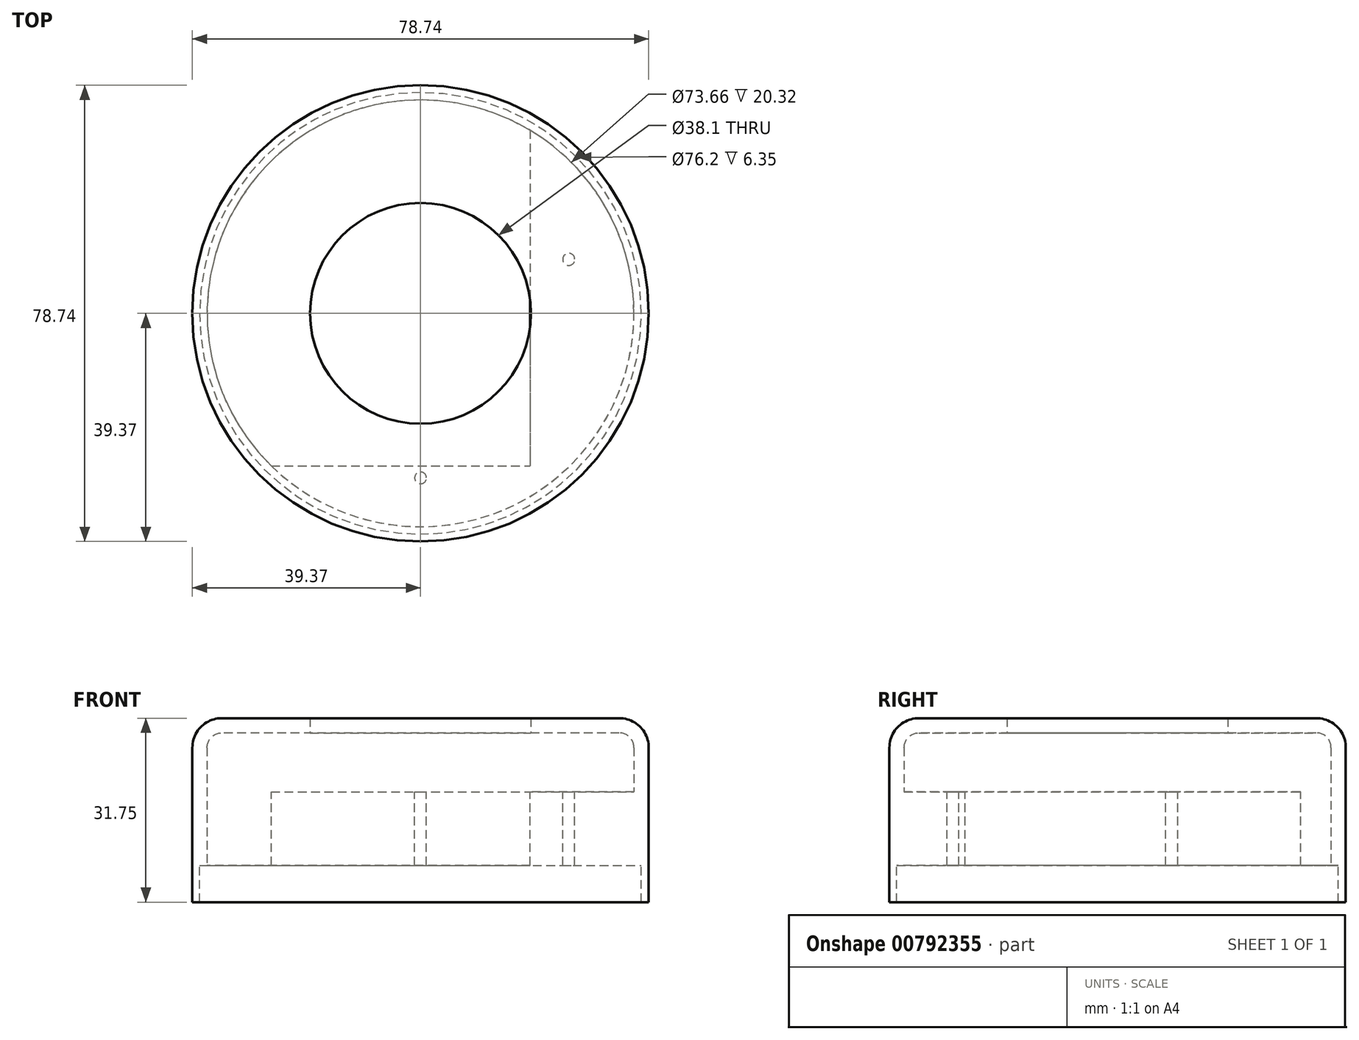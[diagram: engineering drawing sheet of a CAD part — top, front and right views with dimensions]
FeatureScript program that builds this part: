
annotation { "Feature Type Name" : "Feature", "Feature Type Description" : "" }
export const myFeature = defineFeature(function(context is Context, id is Id, definition is map)
    precondition{}
    {
        {
            var Q0;
            Q0=qCreatedBy(makeId("Top.planeOp"),FACE);
            var sketch = newSketch(context, id + "F0", { "sketchPlane" : qUnion([Q0])});
            skCircle(sketch, "E0", {"center": v(0, 0) * mm, "radius": 39.37 * mm});
            skSolve(sketch);
        }
        {
            var Q0;
            Q0 = qSketchRegion(id + "F0", true);
            extrude(context, id + "F1", {"entities" : qUnion([Q0]), "depth" : 12.7 * mm, "offsetDistance" : 25.4 * mm});
        }
        {
            var Q0;
            Q0=makeQuery(id+"F1.opExtrude","CAP_FACE",FACE,{"disambiguationData":[OSD([sQuery(id+"F0.wireOp",EDGE,"E0")])],"isStart":true});
            shell(context, id + "F2", {"entities" : qUnion([Q0]), "thickness" : 2.54 * mm});
        }
        {
            var Q0;
            Q0=makeQuery(id+"F1.opExtrude","CAP_EDGE",EDGE,{"disambiguationData":[OSD([sQuery(id+"F0.wireOp",EDGE,"E0")])],"isStart":false});
            fillet(context, id + "F3", {"entities" : qUnion([Q0]), "radius" : 5.08 * mm, "tangentPropagation" : true, "allowEdgeOverflow" : false});
        }
        {
            var Q0;
            Q0=makeQuery(id+"F0arPh6gx08AXpp_1.opExtrude","CAP_EDGE",EDGE,{"disambiguationData":[OSD([sQuery(id+"FFaWsDePzQ0D9wn_1.wireOp",EDGE,"ae57389e-1940-4f7f-8b4d-1324cf397c20.2.0")])],"isStart":true});
            var Q1;
            Q1=makeQuery(id+"F0arPh6gx08AXpp_1.opExtrude","CAP_EDGE",EDGE,{"disambiguationData":[OSD([sQuery(id+"FFaWsDePzQ0D9wn_1.wireOp",EDGE,"ae57389e-1940-4f7f-8b4d-1324cf397c20.1.0")])],"isStart":true});
            var Q2;
            Q2=makeQuery(id+"F0arPh6gx08AXpp_1.opExtrude","CAP_EDGE",EDGE,{"disambiguationData":[OSD([sQuery(id+"FFaWsDePzQ0D9wn_1.wireOp",EDGE,"ae57389e-1940-4f7f-8b4d-1324cf397c20.3.0")])],"isStart":true});
            var Q3;
            Q3=makeQuery(id+"F0arPh6gx08AXpp_1.opExtrude","CAP_EDGE",EDGE,{"disambiguationData":[OSD([sQuery(id+"FFaWsDePzQ0D9wn_1.wireOp",EDGE,"xz74w6c5-Paq0-shCl-McQr-9mFM74ZJmCNI")])],"isStart":true});
            var Q4;
            {var subQ0=sQuery(id+"F0.wireOp",EDGE,"E0");Q4=makeQuery(id+"F2.opShell","OFFSET_EDGE",EDGE,{"disambiguationData":[OSD([subQ0]),TDD([makeQuery(id+"F1.opExtrude","CAP_EDGE",EDGE,{"disambiguationData":[OSD([subQ0])],"isStart":false})])]});}
            fillet(context, id + "F4", {"entities" : qUnion([Q0, Q1, Q2, Q3, Q4]), "radius" : 2.54 * mm, "tangentPropagation" : true, "allowEdgeOverflow" : false});
        }
        {
            var Q0;
            {var subQ0=sQuery(id+"F0.wireOp",EDGE,"E0");Q0=makeQuery(id+"F0arPh6gx08AXpp_1.boolean.opBoolean","SPLIT",FACE,{"disambiguationData":[TD([makeQuery(id+"F0arPh6gx08AXpp_1.opExtrude","SWEPT_FACE",FACE,{"disambiguationData":[OSD([sQuery(id+"FFaWsDePzQ0D9wn_1.wireOp",EDGE,"xz74w6c5-Paq0-shCl-McQr-9mFM74ZJmCNI")])]})])],"derivedFrom":makeQuery(id+"F2.opShell","OFFSET_FACE",FACE,{"disambiguationData":[OSD([subQ0]),TDD([makeQuery(id+"F1.opExtrude","CAP_FACE",FACE,{"disambiguationData":[OSD([subQ0])],"isStart":false})])]})});}
            var sketch = newSketch(context, id + "F5", { "sketchPlane" : qUnion([Q0])});
            skCircle(sketch, "E1", {"center": v(0, 0) * mm, "radius": 19.05 * mm});
            skSolve(sketch);
        }
        {
            var Q0;
            Q0 = qSketchRegion(id + "F5", true);
            extrude(context, id + "F6", {"entities" : qUnion([Q0]), "operationType" : NewBodyOperationType.REMOVE, "oppositeDirection" : true, "depth" : 25.4 * mm, "offsetDistance" : 25.4 * mm});
        }
        {
            var Q0;
            Q0=makeQuery(id+"F1.opExtrude","CAP_FACE",FACE,{"disambiguationData":[OSD([sQuery(id+"F0.wireOp",EDGE,"E0")])],"isStart":true});
            var sketch = newSketch(context, id + "F7", { "sketchPlane" : qUnion([Q0])});
            skCircle(sketch, "E2", {"center": v(0, 0) * mm, "radius": 39.37 * mm});
            skLineSegment(sketch, "E3", {"start": v(-25.77, 26.31) * mm, "end": v(18.92, 26.31) * mm});
            skCircle(sketch, "E4", {"center": v(0, 28.4) * mm, "radius": 1.02 * mm});
            skCircle(sketch, "E5", {"center": v(25.58, -9.32) * mm, "radius": 1.04 * mm});
            skLineSegment(sketch, "E6", {"start": v(18.92, -31.6) * mm, "end": v(18.92, 26.31) * mm});
            skArc(sketch, "E7", {"start": v(18.92, -31.6) * mm, "mid": v(-29.16, -22.5) * mm, "end": v(-25.77, 26.31) * mm});
            skSolve(sketch);
        }
        {
            var Q0;
            Q0 = qSketchRegion(id + "F7", true);
            extrude(context, id + "F8", {"entities" : qUnion([Q0]), "operationType" : NewBodyOperationType.ADD, "depth" : 12.7 * mm, "offsetDistance" : 25.4 * mm});
        }
        {
            var Q0;
            Q0=makeQuery(id+"F8.opExtrude","CAP_FACE",FACE,{"disambiguationData":[OSD([sQuery(id+"F7.wireOp",EDGE,"E2"),sQuery(id+"F7.wireOp",EDGE,"E3"),sQuery(id+"F7.wireOp",EDGE,"E4"),sQuery(id+"F7.wireOp",EDGE,"E5"),sQuery(id+"F7.wireOp",EDGE,"E6"),sQuery(id+"F7.wireOp",EDGE,"E7")])],"isStart":false});
            var sketch = newSketch(context, id + "F9", { "sketchPlane" : qUnion([Q0])});
            skCircle(sketch, "E8", {"center": v(0, 0) * mm, "radius": 39.37 * mm});
            skCircle(sketch, "E9", {"center": v(0, 0) * mm, "radius": 38.1 * mm});
            skSolve(sketch);
        }
        {
            var Q0;
            Q0 = qSketchRegion(id + "F9", true);
            extrude(context, id + "F10", {"entities" : qUnion([Q0]), "operationType" : NewBodyOperationType.ADD, "depth" : 6.35 * mm, "offsetDistance" : 25.4 * mm});
        }
    });
